# Revit family: GRAS_HW-19N-KP-20-30 Mirror
name_source: partatom
category: Osprzęt hydrauliczny
revit_build: Autodesk Revit 2018 (Build: 20190510_1515(x64)
units: mm (PartAtom-declared; Revit-internal decimal feet)

## family parameters
Obiekt nadrzędny = Powierzchnia
Punkt obliczania pomieszczeń = Nie
Tnij formami wycięć po wczytaniu = Nie
Typ części = Normalny
Współdzielony = Nie
Wymiar okrągłego złącza = Użyj średnicy

## types (1)
- HW-19N-KP-20/30 Mirror
    Cabinet depth = 170 mm  [stored 0.557743 ft]
    Cabinet height = 990 mm  [stored 3.24803 ft]
    Cabinet material = AISI304 - Mirror
    Cabinet width = 680 mm  [stored 2.23097 ft]
    D1 = 85 mm  [stored 0.278871 ft]
    D2 = 85 mm  [stored 0.278871 ft]
    DN = 19 mm  [stored 0.062336 ft]
    Domyślna rzędna = 0 mm  [stored 0 ft]
    Flow = 35.0 L/s
    H1 = 100 mm  [stored 0.328084 ft]
    K Factor = 42
    Model = HW-19N-KP-20/30 Mirror
    Opis = https://gras.pl
    Producent = GRAS PPPH
    URL = http://www.gras.pl
    W1 = 100 mm  [stored 0.328084 ft]
    W2 = 100 mm  [stored 0.328084 ft]

note: [stored X ft] marks values corroborated as IEEE doubles in the binary element streams (Revit-internal decimal feet)

## geometry (parser evidence)
native form markers: Blend x8
no freeform markers — native parametric forms only
